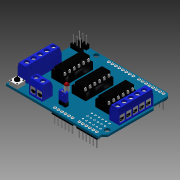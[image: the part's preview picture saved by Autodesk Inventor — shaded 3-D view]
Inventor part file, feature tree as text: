
AUTODESK INVENTOR PART (.ipt)
format: ipt  version: 2014 (Build 180170000, 170)  size: 3,072,000 bytes
history: native  units: in
note: dims shown in document units (in); Inventor stores cm internally (conversion verified against a paired STEP export)
features: sketch x75, extrude x67, plane x26, projected_geometry x21, fillet x18, pattern_linear x12, chamfer x6, loft x4
ambient origin geometry x8: Origin, YZ Plane, XZ Plane, XY Plane, X Axis, Y Axis, Z Axis, Center Point
bodies: Solid1 (feature_tree)
feature tree (229):
  extrude  "Extrusion1"  Depth=2.088in
  extrude  "Extrusion2"  TaperAngle=135.0deg  [1 undecoded]
  extrude  "Extrusion3"  Depth=0.1in
  extrude  "Extrusion4"  Depth=0.092in
  extrude  "Extrusion5"  Depth=0.061in TaperAngle=0.0deg
  extrude  "Extrusion6"  Depth=0.021in
  extrude  "Extrusion7"  Depth=0.052in
  extrude  "Extrusion8"  Depth=0.061in TaperAngle=0.0deg
  extrude  "Extrusion9"  Depth=0.975in
  fillet  "Fillet2"  Radius=0.384in
  extrude  "Extrusion10"  Depth=0.065in
  extrude  "Extrusion11"  Depth=0.06in
  extrude  "Extrusion12"  Depth=0.3in
  plane  "Work Plane1"
  extrude  "Extrusion13"  Depth=0.03in
  sketch  "Sketch16"  dims[d36=0.13in d37=0.06in]
  plane  "Work Plane2"
  loft  "Loft1"
  extrude  "Extrusion14"  Depth=0.03in
  pattern_linear  "Rectangular Pattern1"  Count1=5 Spacing1=0.19in
  extrude  "Extrusion15"  Depth=0.03in
  extrude  "Extrusion16"  Depth=0.161in
  extrude  "Extrusion17"  Depth=0.12in TaperAngle=0.0deg
  fillet  "Fillet3"  Radius=0.04in
  extrude  "Extrusion18"  Depth=0.01in
  extrude  "Extrusion19"  Depth=0.025in TaperAngle=0.0deg
  extrude  "Extrusion20"  Depth=0.075in TaperAngle=0.0deg
  plane  "Work Plane11"
  extrude  "Extrusion21"  Depth=0.04in
  sketch  "Sketch26"  dims[d51=0.0135in]
  plane  "Work Plane12"
  loft  "Loft2"
  extrude  "Extrusion22"  Depth=0.079in
  pattern_linear  "Rectangular Pattern2"  Spacing1=0.085in  [1 undecoded]
  extrude  "Extrusion23"  Depth=0.1in
  extrude  "Extrusion24"  Depth=0.06in
  extrude  "Extrusion25"  Depth=0.025in
  fillet  "Fillet5"  Radius=0.035in
  extrude  "Extrusion26"  Depth=0.035in
  extrude  "Extrusion27"  Depth=0.02in
  extrude  "Extrusion28"  TaperAngle=0.0deg  [1 undecoded]
  plane  "Work Plane21"
  extrude  "Extrusion29"  TaperAngle=0.0deg  [1 undecoded]
  sketch  "Sketch36"  dims[d63=0.125in]
  plane  "Work Plane22"
  loft  "Loft3"
  extrude  "Extrusion30"  Depth=0.19in
  pattern_linear  "Rectangular Pattern3"  Spacing1=0.0785in  [1 undecoded]
  extrude  "Extrusion31"  Depth=0.06in
  fillet  "Fillet6"  Radius=0.023in
  extrude  "Extrusion32"  Depth=0.13in
  chamfer  "Chamfer1"  Distance=0.03in
  extrude  "Extrusion33"  Depth=0.12in TaperAngle=0.0deg
  fillet  "Fillet7"  Radius=0.04in
  pattern_linear  "Rectangular Pattern4"  Spacing1=0.01in  [1 undecoded]
  extrude  "Extrusion34"  Depth=0.06in
  fillet  "Fillet8"  Radius=0.2in
  extrude  "Extrusion35"  Depth=0.025in TaperAngle=0.0deg
  chamfer  "Chamfer2"  Distance=0.12in
  extrude  "Extrusion36"  Depth=0.075in TaperAngle=0.0deg
  fillet  "Fillet9"  Radius=0.015in
  pattern_linear  "Rectangular Pattern5"  Spacing1=0.04in  [1 undecoded]
  extrude  "Extrusion37"  Depth=0.06in
  fillet  "Fillet10"  Radius=0.015in
  extrude  "Extrusion38"  Depth=0.06in
  chamfer  "Chamfer3"  Distance=0.12in
  extrude  "Extrusion39"  Depth=0.25in TaperAngle=0.0deg
  fillet  "Fillet11"  Radius=0.085in
  pattern_linear  "Rectangular Pattern6"  Spacing1=0.09in  [1 undecoded]
  extrude  "Extrusion40"  Depth=0.005in TaperAngle=0.0deg
  fillet  "Fillet12"  [1 undecoded]
  extrude  "Extrusion41"  TaperAngle=135.0deg  [1 undecoded]
  chamfer  "Chamfer4"  Distance=0.075in
  extrude  "Extrusion42"  Depth=0.085in TaperAngle=0.0deg
  fillet  "Fillet13"  Radius=0.015in
  pattern_linear  "Rectangular Pattern7"  Spacing1=0.015in  [1 undecoded]
  extrude  "Extrusion43"  Depth=0.015in
  fillet  "Fillet14"  Radius=0.17in
  extrude  "Extrusion44"  Depth=0.05in
  chamfer  "Chamfer5"  Distance=0.025in
  extrude  "Extrusion45"  Depth=0.035in
  fillet  "Fillet15"  Radius=0.035in
  pattern_linear  "Rectangular Pattern8"  Spacing1=0.02in  [1 undecoded]
  extrude  "Extrusion46"  TaperAngle=0.0deg  [1 undecoded]
  fillet  "Fillet16"  [1 undecoded]
  extrude  "Extrusion47"  Depth=0.02in TaperAngle=0.0deg
  fillet  "Fillet17"  Radius=0.19in
  pattern_linear  "Rectangular Pattern9"  Spacing1=0.175in  [1 undecoded]
  extrude  "Extrusion49"  Depth=0.05in
  extrude  "Extrusion50"  Depth=0.099in
  plane  "Work Plane25"
  extrude  "Extrusion51"  Depth=0.099in
  extrude  "Extrusion52"  Depth=0.09in TaperAngle=0.0deg
  extrude  "Extrusion53"  Depth=0.015in
  extrude  "Extrusion54"  Depth=0.02in
  extrude  "Extrusion55"  Depth=0.02in
  extrude  "Extrusion56"  Depth=0.25in TaperAngle=0.0deg
  fillet  "Fillet18"  Radius=0.005in
  sketch  "Sketch66"  dims[d104=0.023in d105=0.12in d106=0.0in d107=0.04in]
  plane  "Work Plane26"
  loft  "Loft4"
  extrude  "Extrusion57"  Depth=0.03in
  chamfer  "Chamfer6"  Distance=0.1in
  pattern_linear  "Rectangular Pattern10"  Spacing1=0.1in  [1 undecoded]
  extrude  "Extrusion58"  Depth=0.1in
  extrude  "Extrusion59"  Depth=0.1in
  pattern_linear  "Rectangular Pattern11"  Spacing1=0.04in  [1 undecoded]
  extrude  "Extrusion60"  Depth=0.015in
  extrude  "Extrusion61"  Depth=0.02in
  extrude  "Extrusion62"  TaperAngle=0.0deg  [1 undecoded]
  extrude  "Extrusion63"  Depth=0.005in TaperAngle=45.0deg
  extrude  "Extrusion64"  Depth=0.04in TaperAngle=0.0deg
  extrude  "Extrusion65"  Depth=0.03in
  extrude  "Extrusion66"  Depth=0.101in
  extrude  "Extrusion67"  Depth=0.1in
  fillet  "Fillet20"  Radius=0.025in
  pattern_linear  "Rectangular Pattern12"  Spacing1=0.04in  [1 undecoded]
  extrude  "Extrusion68"  Depth=0.015in
  fillet  "Fillet21"  Radius=0.02in
  sketch  "Sketch1"  dims[d2=2.64in d3=2.088in]
  sketch  "Sketch3"  dims[d4=135.0deg d6=0.075in d7=135.0deg]
  sketch  "Sketch4"  dims[d8=135.0deg d9=0.092in d10=0.1in]
  sketch  "Sketch6"  dims[d11=1.5in d12=0.092in]
  sketch  "Sketch7"  dims[d13=135.0deg d14=0.061in d15=0.0in]
  sketch  "Sketch8"  dims[d17=0.141in d18=0.021in]
  sketch  "Sketch9"  dims[d19=0.525in d20=0.052in]
  sketch  "Sketch10"  dims[d21=0.225in d22=0.061in d23=0.0in]
  sketch  "Sketch11"  dims[d24=0.291in d25=0.975in d26=0.384in]
  sketch  "Sketch12"  dims[d27=0.065in d28=0.594in]
  projected_geometry  "Projected Loop1"
  sketch  "Sketch13"  dims[d29=0.03in d30=0.06in]
  sketch  "Sketch14"  dims[d31=0.533in d32=0.3in]
  sketch  "Sketch15"  dims[d33=0.4in d34=0.0in d35=0.03in]
  projected_geometry  "Projected Loop2"
  sketch  "Sketch17"  dims[d38=1.0in d39=0.0in d40=0.03in]
  sketch  "Sketch18"  dims[d41=0.06in]
  plane  "Work Plane3"
  plane  "Work Plane4"
  plane  "Work Plane5"
  plane  "Work Plane6"
  plane  "Work Plane7"
  plane  "Work Plane8"
  plane  "Work Plane9"
  plane  "Work Plane10"
  sketch  "Sketch19"  dims[d42=0.13in]
  sketch  "Sketch20"  dims[d43=1.0in d44=0.0in]
  sketch  "Sketch21"  dims[d45=0.06in]
  sketch  "Sketch22"  dims[d46=0.03in]
  projected_geometry  "Projected Loop3"
  sketch  "Sketch23"  dims[d47=0.13in]
  sketch  "Sketch24"  dims[d48=1.0in d49=0.0in]
  sketch  "Sketch25"  dims[d50=0.13in]
  projected_geometry  "Projected Loop4"
  sketch  "Sketch27"  dims[d52=0.035in]
  sketch  "Sketch28"  dims[d53=0.03in]
  plane  "Work Plane13"
  plane  "Work Plane14"
  plane  "Work Plane15"
  plane  "Work Plane16"
  plane  "Work Plane17"
  plane  "Work Plane18"
  plane  "Work Plane19"
  plane  "Work Plane20"
  sketch  "Sketch29"  dims[d54=0.022in]
  sketch  "Sketch30"  dims[d55=0.12in d56=0.0in]
  sketch  "Sketch31"  dims[d57=0.17in]
  sketch  "Sketch32"  dims[d58=0.2in]
  sketch  "Sketch33"  dims[d59=0.03in]
  sketch  "Sketch34"  dims[d60=0.01in]
  sketch  "Sketch35"  dims[d61=0.025in d62=0.0in]
  projected_geometry  "Projected Loop5"
  projected_geometry  "Projected Loop6"
  sketch  "Sketch37"  dims[d64=0.075in d65=0.0in]
  sketch  "Sketch38"  dims[d66=0.015in]
  plane  "Work Plane23"
  plane  "Work Plane24"
  sketch  "Sketch39"  dims[d67=0.04in]
  sketch  "Sketch40"  dims[d68=0.2405in]
  sketch  "Sketch41"  dims[d69=0.015in d70=0.0in]
  sketch  "Sketch42"  dims[d71=0.12in]
  sketch  "Sketch43"  dims[d72=0.12in]
  sketch  "Sketch44"  dims[d73=0.25in d74=0.0in]
  sketch  "Sketch45"  dims[d75=0.085in]
  sketch  "Sketch46"  dims[d76=0.09in]
  sketch  "Sketch47"  dims[d77=0.005in d78=0.0in]
  projected_geometry  "Projected Loop7"
  sketch  "Sketch48"  dims[d79=0.0in]
  sketch  "Sketch50"  dims[d80=135.0deg]
  sketch  "Sketch51"  dims[d81=0.075in]
  sketch  "Sketch52"  dims[d82=0.085in d83=0.0in]
  sketch  "Sketch53"  dims[d84=0.05in]
  projected_geometry  "Projected Loop8"
  sketch  "Sketch54"  dims[d85=0.17in]
  sketch  "Sketch55"  dims[d86=0.1in]
  projected_geometry  "Projected Loop9"
  projected_geometry  "Projected Loop10"
  sketch  "Sketch56"  dims[d87=0.02in]
  projected_geometry  "Projected Loop11"
  sketch  "Sketch58"  dims[d88=0.035in]
  projected_geometry  "Projected Loop13"
  sketch  "Sketch59"  dims[d89=0.035in]
  sketch  "Sketch60"  dims[d90=0.035in]
  sketch  "Sketch61"  dims[d91=0.0in d92=90.0deg]
  projected_geometry  "Projected Loop14"
  sketch  "Sketch62"  dims[d93=0.0in d94=90.0deg]
  projected_geometry  "Projected Loop15"
  sketch  "Sketch63"  dims[d95=0.02in d96=0.0in d97=1.9685in d99=0.19in]
  sketch  "Sketch64"  dims[d100=0.13in d101=0.03in]
  sketch  "Sketch65"  dims[d102=0.0785in d103=0.161in]
  projected_geometry  "Projected Loop16"
  sketch  "Sketch67"  dims[d108=0.01in d109=0.17in]
  sketch  "Sketch68"  dims[d110=0.2in d111=0.025in d112=0.0in]
  sketch  "Sketch69"  dims[d113=0.12in d114=0.075in d115=0.0in]
  sketch  "Sketch70"  dims[d116=0.015in d117=0.04in]
  sketch  "Sketch71"  dims[d118=0.2405in d119=0.015in d120=0.0in]
  sketch  "Sketch72"  dims[d121=0.12in d122=0.079in]
  projected_geometry  "Projected Loop17"
  projected_geometry  "Projected Loop18"
  sketch  "Sketch73"  dims[d123=0.25in d124=0.0in]
  sketch  "Sketch74"  dims[d125=0.085in]
  projected_geometry  "Projected Loop19"
  sketch  "Sketch75"  dims[d126=0.09in]
  projected_geometry  "Projected Loop20"
  sketch  "Sketch76"  dims[d127=0.005in d128=0.0in]
  projected_geometry  "Projected Loop21"
  sketch  "Sketch77"  dims[d129=0.0in]
  sketch  "Sketch78"  dims[d130=135.0deg]
  projected_geometry  "Projected Loop22"
  sketch  "Sketch79"  dims[d131=0.075in d132=0.085in d133=0.0in d134=0.1in d136=0.17in d137=0.025in d138=0.035in d139=0.035in d140=0.02in d141=0.0in d142=90.0deg d143=0.0in d144=90.0deg d145=0.02in d146=0.0in d147=1.9685in d149=0.19in d150=0.0785in d151=0.161in d152=0.023in d153=0.13in d154=0.03in d155=0.12in d156=0.0in d157=0.04in d158=0.01in d159=0.17in d160=0.2in d161=0.025in d162=0.0in d163=0.12in d164=0.075in d165=0.0in d167=0.015in d168=0.04in d169=0.2405in d170=0.015in d171=0.0in d172=0.121in d173=0.12in d174=0.25in d175=0.0in d176=0.085in d177=0.09in d178=0.005in d179=0.0in d180=0.0in d181=135.0deg d182=0.075in d183=0.085in d184=0.0in d185=0.015in d186=0.015in d187=0.015in d188=0.17in d189=0.05in d190=0.025in d191=0.035in d192=0.035in d193=0.02in d194=0.0in d195=90.0deg d196=0.0in d197=90.0deg d198=0.02in d199=0.0in d200=0.7874in d202=0.19in d203=0.175in d204=0.05in d205=0.099in d206=0.099in d207=0.09in d208=0.0in d209=0.015in d210=0.02in d211=0.02in d212=0.25in d213=0.0in d214=0.005in d215=0.125in d216=45.0deg d217=0.04in d218=0.0in d219=0.03in d220=2.3622in d222=0.1in d223=0.1in d224=0.1in d225=0.1in d226=0.04in d227=0.0in d228=0.015in d229=0.02in d230=0.0in d231=0.0in d232=0.005in d233=0.125in d234=45.0deg d235=0.04in d236=0.0in d237=0.03in d238=2.3622in d240=0.101in d241=0.1in d242=0.025in d243=0.04in d244=0.0in d245=0.015in d246=0.02in d247=0.02in d248=0.04in d249=0.0in d250=0.005in d251=0.125in d252=45.0deg d253=0.04in d254=0.0in d255=0.03in d256=0.08in d257=0.1in d258=3.1496in d260=0.1003in d261=0.1in d262=0.065in d263=0.0in d264=0.0in d265=0.015in d266=0.02in d267=0.04in d268=0.0in d269=0.005in d270=0.125in d271=45.0deg d272=0.04in d273=0.0in d274=0.03in d275=3.1496in d277=0.1003in d278=0.1in d279=0.015in d280=0.025in d281=0.065in d282=0.103in d283=0.0in d284=0.015in d285=0.02in d286=0.23in d287=0.0in d288=0.005in d289=0.125in d290=45.0deg d291=0.04in d292=0.0in d293=0.03in d294=1.1811in d296=0.101in d297=0.1in d298=0.1in d299=0.04in d300=0.0in d301=0.015in d302=0.02in d303=0.04in d304=0.0in d305=0.03in d306=0.7874in d308=0.101in d311=0.19in d312=0.088in d313=0.0055in d314=0.0055in d315=0.006in d316=0.006in d317=0.235in d318=0.0in d319=0.0675in d320=0.1in d321=0.235in d322=0.0in d323=-0.004in d324=0.1755in d325=0.0073in d326=0.0073in d327=0.075in d328=0.02in d329=0.0in d330=0.03in d331=0.03in d332=0.03in d333=0.03in d334=0.2in d335=0.0in d336=0.005in d337=0.005in d338=0.005in d339=0.005in d340=0.005in d341=0.005in d342=0.005in d343=0.02in d344=0.0in d345=0.01in d346=0.07in d347=0.2375in d348=0.11in d349=0.0in d350=0.128in d351=0.0385in d352=0.0in d354=0.01in d355=0.01in d356=0.01in d357=0.01in d358=0.04in d359=0.02in d360=0.0in d361=0.02in d362=0.12in d363=0.06in d364=0.03in d365=0.03in d366=0.025in d367=0.01in d368=0.0in d369=90.0deg d370=0.0in d371=90.0deg d372=0.02in d373=0.0in d374=0.005in d375=0.125in d376=45.0deg d377=0.7874in d379=0.18in d380=0.7874in d382=0.233in d384=0.24in d385=0.22in d386=0.02in d387=0.02in d388=0.0in d389=0.05in d390=0.001in d391=0.0in d392=2.3622in d394=0.101in d395=1.1811in d397=0.13in d399=0.7in d400=0.5in d401=0.185in d402=0.2785in d403=0.2785in d404=0.8in d405=0.4in d406=0.2in d407=0.0in d408=0.24in d409=0.78in d410=0.01in d411=0.01in d412=0.01in d413=0.08in d414=0.08in d415=0.08in d416=0.08in d417=0.12in d418=0.0in d419=0.025in d420=0.05in d421=0.05in d422=0.03in d423=0.0in d425=0.03in d426=0.0in d427=0.03in d428=0.0in d429=0.03in d430=0.0in d431=0.025in d432=0.05in d433=0.05in d434=0.03in d435=0.0in d436=0.03in d437=0.0in d438=0.03in d439=2.3622in d441=0.1355in d442=0.64in d443=0.66in d444=0.12in d445=0.2in d446=0.0in d447=0.06in]
note: 19 required parameter values undecoded (feature->parameter linkage not recoverable at this tier; creation-order binding heuristic only, values carry confidence <= 0.55)
